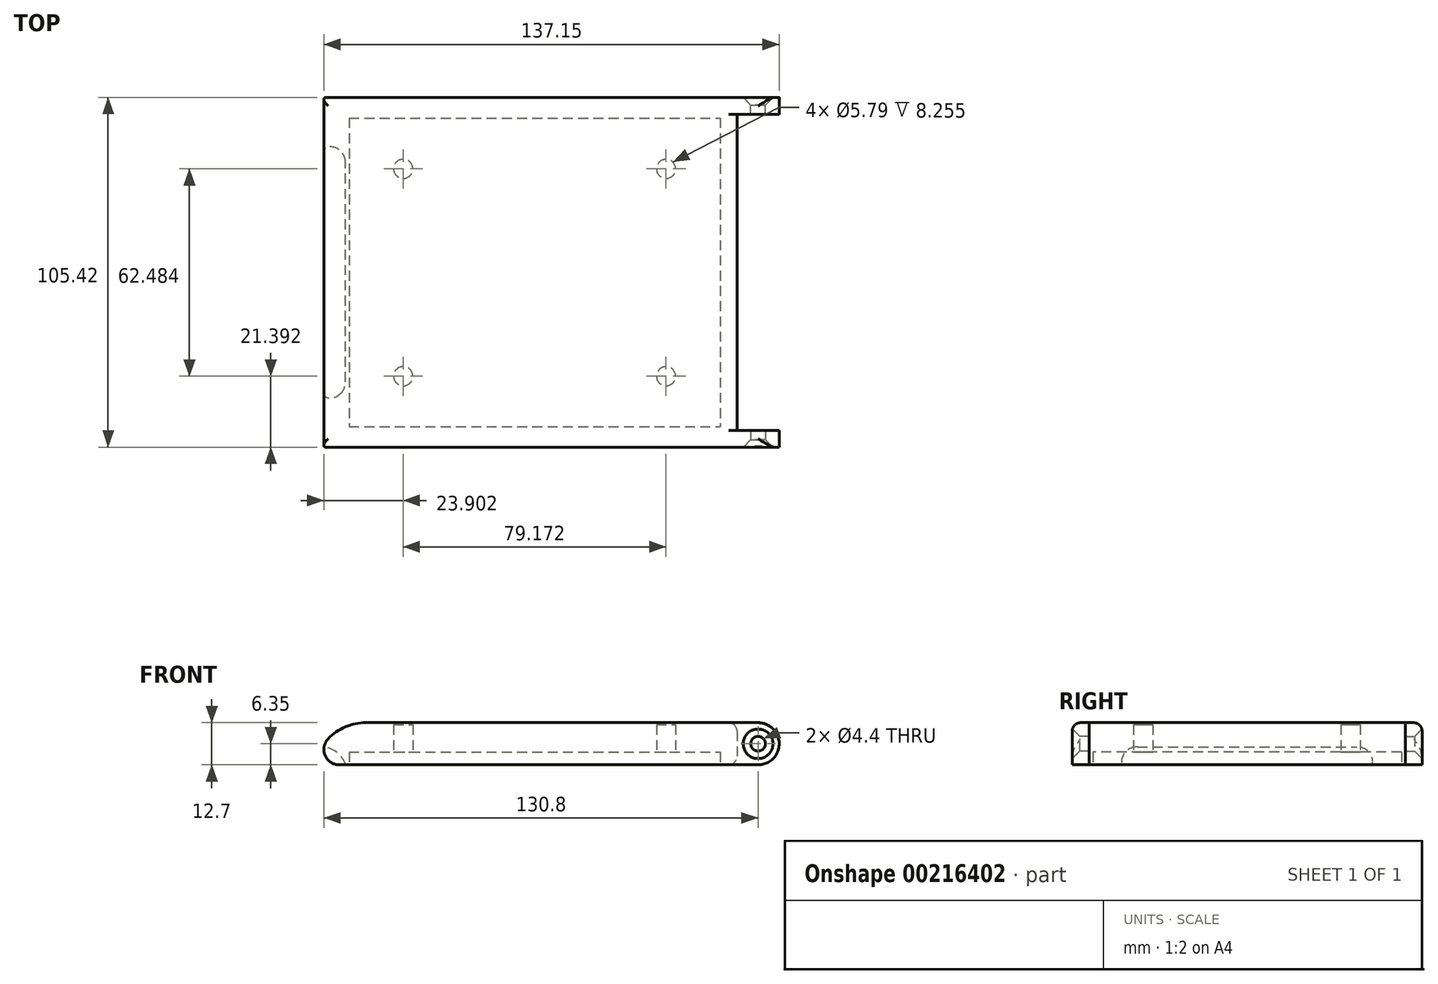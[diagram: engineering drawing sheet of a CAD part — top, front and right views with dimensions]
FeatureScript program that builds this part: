
annotation { "Feature Type Name" : "Feature", "Feature Type Description" : "" }
export const myFeature = defineFeature(function(context is Context, id is Id, definition is map)
    precondition{}
    {
        {
            var Q0;
            Q0=qCreatedBy(makeId("Front.planeOp"),FACE);
            var sketch = newSketch(context, id + "F0", { "sketchPlane" : qUnion([Q0])});
            skLineSegment(sketch, "E0", {"start": v(-6.35, 0) * mm, "end": v(-132.53, 0) * mm});
            skLineSegment(sketch, "E1", {"start": v(0, 6.35) * mm, "end": v(0, 6.35) * mm});
            skPoint(sketch, "E2.visualSharp", {"position": v(0, 12.7) * mm});
            skArc(sketch, "E2.filletArc", {"start": v(0, 6.35) * mm, "mid": v(-1.86, 10.84) * mm, "end": v(-6.35, 12.7) * mm});
            skPoint(sketch, "E3.visualSharp", {"position": v(0, 0) * mm});
            skArc(sketch, "E3.filletArc", {"start": v(-6.35, 0) * mm, "mid": v(-1.86, 1.86) * mm, "end": v(0, 6.35) * mm});
            skLineSegment(sketch, "E4", {"start": v(-6.35, 12.7) * mm, "end": v(-124.46, 12.7) * mm});
            skArc(sketch, "E5", {"start": v(-135.88, 7.81) * mm, "mid": v(-136.78, 2.8) * mm, "end": v(-132.53, 0) * mm});
            skArc(sketch, "E6", {"start": v(-124.46, 12.7) * mm, "mid": v(-130.67, 11.43) * mm, "end": v(-135.88, 7.81) * mm});
            skSolve(sketch);
        }
        {
            var Q0;
            Q0 = qSketchRegion(id + "F0", true);
            extrude(context, id + "F1", {"entities" : qUnion([Q0]), "endBound" : BoundingType.SYMMETRIC, "oppositeDirection" : true, "depth" : 105.4 * mm});
        }
        {
            var Q0;
            Q0=makeQuery(id+"F1.opExtrude","CAP_FACE",FACE,{"disambiguationData":[OSD([sQuery(id+"F0.wireOp",EDGE,"E0"),sQuery(id+"F0.wireOp",EDGE,"E1"),sQuery(id+"F0.wireOp",EDGE,"HZy6QrKH-Mdw4-o4Dm-VMrE-zzrVWmDgLelF"),sQuery(id+"F0.wireOp",EDGE,"t4Bq1xRU-PNGr-nmEO-KA5W-6uztIBIaK37j"),sQuery(id+"F0.wireOp",EDGE,"E2.filletArc"),sQuery(id+"F0.wireOp",EDGE,"E3.filletArc")])],"isStart":false});
            var sketch = newSketch(context, id + "F2", { "sketchPlane" : qUnion([Q0])});
            skPoint(sketch, "E7", {"position": v(6.35, 6.35) * mm});
            skSolve(sketch);
        }
        {
            var Q0;
            Q0=sQuery(id+"F2.wireOp",VERTEX,"E7");
            var Q1;
            Q1=makeQuery(id+"F1.opExtrude","SWEPT_BODY",BODY,{"disambiguationData":[OSD([sQuery(id+"F0.wireOp",EDGE,"E0"),sQuery(id+"F0.wireOp",EDGE,"E1"),sQuery(id+"F0.wireOp",EDGE,"HZy6QrKH-Mdw4-o4Dm-VMrE-zzrVWmDgLelF"),sQuery(id+"F0.wireOp",EDGE,"t4Bq1xRU-PNGr-nmEO-KA5W-6uztIBIaK37j"),sQuery(id+"F0.wireOp",EDGE,"E2.filletArc"),sQuery(id+"F0.wireOp",EDGE,"E3.filletArc")])]});
            hole(context, id + "F3", {"style" : HoleStyle.C_SINK, "endStyle" : HoleEndStyle.BLIND, "standardTappedOrClearance" : lookupTablePath({ "standard" : "ISO", "fit" : "Normal", "size" : "M4", "type" : "Clearance" }), "standardBlindInLast" : lookupTablePath({ "fit" : "Standard", "standard" : "ISO", "size" : "M4", "type" : "Clearance" }), "holeDiameter" : 4.4 * mm, "cSinkDiameter" : 8.96 * mm, "cSinkAngle" : 90 * degree, "holeDepth" : 25.4 * mm, "tappedDepth" : 3.96 * mm, "tapClearance" : 3, "locations" : qUnion([Q0]), "scope" : qUnion([Q1])});
        }
        {
            var Q0;
            Q0=qCreatedBy(makeId("Front.planeOp"),FACE);
            var sketch = newSketch(context, id + "F4", { "sketchPlane" : qUnion([Q0])});
            skLineSegment(sketch, "E8.bottom", {"start": v(-12.7, 13.86) * mm, "end": v(12.7, 13.86) * mm});
            skLineSegment(sketch, "E8.top", {"start": v(-12.7, -13.86) * mm, "end": v(12.7, -13.86) * mm});
            skLineSegment(sketch, "E8.left", {"start": v(-12.7, 13.86) * mm, "end": v(-12.7, -13.86) * mm});
            skLineSegment(sketch, "E8.right", {"start": v(12.7, 13.86) * mm, "end": v(12.7, -13.86) * mm});
            skPoint(sketch, "E8.middle", {"position": v(0, 0) * mm});
            skSolve(sketch);
        }
        {
            var Q0;
            Q0 = qSketchRegion(id + "F4", true);
            extrude(context, id + "F5", {"entities" : qUnion([Q0]), "operationType" : NewBodyOperationType.REMOVE, "endBound" : BoundingType.SYMMETRIC, "oppositeDirection" : true, "depth" : 95.25 * mm});
        }
        {
            var Q0;
            Q0=makeQuery(id+"F1.opExtrude","CAP_FACE",FACE,{"disambiguationData":[OSD([sQuery(id+"F0.wireOp",EDGE,"E0"),sQuery(id+"F0.wireOp",EDGE,"E1"),sQuery(id+"F0.wireOp",EDGE,"HZy6QrKH-Mdw4-o4Dm-VMrE-zzrVWmDgLelF"),sQuery(id+"F0.wireOp",EDGE,"t4Bq1xRU-PNGr-nmEO-KA5W-6uztIBIaK37j"),sQuery(id+"F0.wireOp",EDGE,"E2.filletArc"),sQuery(id+"F0.wireOp",EDGE,"E3.filletArc")])],"isStart":true});
            var sketch = newSketch(context, id + "F6", { "sketchPlane" : qUnion([Q0])});
            skPoint(sketch, "E9", {"position": v(-6.35, 6.35) * mm});
            skSolve(sketch);
        }
        {
            var Q0;
            Q0=sQuery(id+"F6.wireOp",VERTEX,"E9");
            var Q1;
            Q1=makeQuery(id+"F1.opExtrude","SWEPT_BODY",BODY,{"disambiguationData":[OSD([sQuery(id+"F0.wireOp",EDGE,"E0"),sQuery(id+"F0.wireOp",EDGE,"E1"),sQuery(id+"F0.wireOp",EDGE,"HZy6QrKH-Mdw4-o4Dm-VMrE-zzrVWmDgLelF"),sQuery(id+"F0.wireOp",EDGE,"t4Bq1xRU-PNGr-nmEO-KA5W-6uztIBIaK37j"),sQuery(id+"F0.wireOp",EDGE,"E2.filletArc"),sQuery(id+"F0.wireOp",EDGE,"E3.filletArc")])]});
            hole(context, id + "F7", {"style" : HoleStyle.C_SINK, "endStyle" : HoleEndStyle.BLIND, "standardTappedOrClearance" : lookupTablePath({ "standard" : "ISO", "fit" : "Normal", "size" : "M4", "type" : "Clearance" }), "standardBlindInLast" : lookupTablePath({ "fit" : "Standard", "standard" : "ISO", "size" : "M4", "type" : "Clearance" }), "holeDiameter" : 4.4 * mm, "cSinkDiameter" : 8.96 * mm, "cSinkAngle" : 90 * degree, "holeDepth" : 25.4 * mm, "tappedDepth" : 3.96 * mm, "tapClearance" : 3, "locations" : qUnion([Q0]), "scope" : qUnion([Q1])});
        }
        {
            var Q0;
            Q0=makeQuery(id+"F1.opExtrude","SWEPT_FACE",FACE,{"disambiguationData":[OSD([sQuery(id+"F0.wireOp",EDGE,"E0")])]});
            var sketch = newSketch(context, id + "F8", { "sketchPlane" : qUnion([Q0])});
            skLineSegment(sketch, "E10.bottom", {"start": v(-129.54, -46.48) * mm, "end": v(-17.78, -46.48) * mm});
            skLineSegment(sketch, "E10.top", {"start": v(-129.54, 46.48) * mm, "end": v(-17.78, 46.48) * mm});
            skLineSegment(sketch, "E10.left", {"start": v(-129.54, -46.48) * mm, "end": v(-129.54, 46.48) * mm});
            skLineSegment(sketch, "E10.right", {"start": v(-17.78, -46.48) * mm, "end": v(-17.78, 46.48) * mm});
            skPoint(sketch, "E11", {"position": v(-17.78, 0) * mm});
            skLineSegment(sketch, "E12", {"start": v(-17.78, 0) * mm, "end": v(-12.7, 0) * mm});
            skSolve(sketch);
        }
        {
            var Q0;
            Q0 = qSketchRegion(id + "F8", true);
            extrude(context, id + "F9", {"entities" : qUnion([Q0]), "operationType" : NewBodyOperationType.REMOVE, "oppositeDirection" : true, "depth" : 3.8 * mm});
        }
        {
            var Q0;
            Q0=makeQuery(id+"F9.boolean.opBoolean","COPY",FACE,{"derivedFrom":makeQuery(id+"F9.opExtrude","CAP_FACE",FACE,{"disambiguationData":[OSD([sQuery(id+"F8.wireOp",EDGE,"E10.bottom"),sQuery(id+"F8.wireOp",EDGE,"E10.top"),sQuery(id+"F8.wireOp",EDGE,"E10.left"),sQuery(id+"F8.wireOp",EDGE,"E10.right")])],"isStart":false})});
            var sketch = newSketch(context, id + "F10", { "sketchPlane" : qUnion([Q0])});
            skPoint(sketch, "E13", {"position": v(-113.25, -31.17) * mm});
            skPoint(sketch, "E14.0.1.0", {"position": v(-113.25, 31.32) * mm});
            skPoint(sketch, "E14.1.0.0", {"position": v(-34.08, -31.17) * mm});
            skPoint(sketch, "E14.1.1.0", {"position": v(-34.08, 31.32) * mm});
            skLineSegment(sketch, "E14.direction1", {"start": v(-113.25, -31.17) * mm, "end": v(-34.08, -31.17) * mm, "construction": true});
            skLineSegment(sketch, "E14.direction2", {"start": v(-113.25, -31.17) * mm, "end": v(-113.25, 31.32) * mm, "construction": true});
            skCircle(sketch, "E15", {"center": v(-113.25, -31.17) * mm, "radius": 2.9 * mm});
            skCircle(sketch, "E16", {"center": v(-113.25, 31.32) * mm, "radius": 2.9 * mm});
            skCircle(sketch, "E17", {"center": v(-34.08, 31.32) * mm, "radius": 2.9 * mm});
            skCircle(sketch, "E18", {"center": v(-34.08, -31.17) * mm, "radius": 2.9 * mm});
            skSolve(sketch);
        }
        {
            var Q0;
            Q0 = qSketchRegion(id + "F10", true);
            extrude(context, id + "F11", {"entities" : qUnion([Q0]), "operationType" : NewBodyOperationType.REMOVE, "oppositeDirection" : true, "depth" : 8.25 * mm});
        }
        {
            var Q0;
            Q0=makeQuery(id+"F1.opExtrude","CAP_EDGE",EDGE,{"disambiguationData":[OSD([sQuery(id+"F0.wireOp",EDGE,"E4")])],"isStart":true});
            var Q1;
            Q1=makeQuery(id+"F1.opExtrude","CAP_EDGE",EDGE,{"disambiguationData":[OSD([sQuery(id+"F0.wireOp",EDGE,"E4")])],"isStart":false});
            var Q2;
            Q2=makeQuery(id+"F1.opExtrude","CAP_EDGE",EDGE,{"disambiguationData":[OSD([sQuery(id+"F0.wireOp",EDGE,"E6")])],"isStart":false});
            var Q3;
            Q3=makeQuery(id+"F1.opExtrude","CAP_EDGE",EDGE,{"disambiguationData":[OSD([sQuery(id+"F0.wireOp",EDGE,"E6")])],"isStart":true});
            fillet(context, id + "F12", {"entities" : qUnion([Q0, Q1, Q2, Q3]), "radius" : 2.54 * mm, "allowEdgeOverflow" : false});
        }
        {
            var Q0;
            Q0=qCreatedBy(makeId("Front.planeOp"),FACE);
            var sketch = newSketch(context, id + "F13", { "sketchPlane" : qUnion([Q0])});
            skLineSegment(sketch, "E19", {"start": v(-130.28, -3.45) * mm, "end": v(-139.17, -3.45) * mm});
            skLineSegment(sketch, "E20", {"start": v(-139.17, -3.45) * mm, "end": v(-139.17, 5.44) * mm});
            skArc(sketch, "E21", {"start": v(-130.28, -3.45) * mm, "mid": v(-132.57, 3.16) * mm, "end": v(-139.17, 5.44) * mm});
            skSolve(sketch);
        }
        {
            var Q0;
            Q0 = qSketchRegion(id + "F13", true);
            extrude(context, id + "F14", {"entities" : qUnion([Q0]), "operationType" : NewBodyOperationType.REMOVE, "endBound" : BoundingType.SYMMETRIC, "depth" : 76.2 * mm});
        }
        {
            var Q0;
            Q0=makeQuery(id+"F14.boolean.opBoolean","COPY",EDGE,{"derivedFrom":makeQuery(id+"F14.opExtrude","CAP_EDGE",EDGE,{"disambiguationData":[OSD([sQuery(id+"F13.wireOp",EDGE,"E21")])],"isStart":true})});
            var Q1;
            Q1=makeQuery(id+"F14.boolean.opBoolean","COPY",EDGE,{"derivedFrom":makeQuery(id+"F14.opExtrude","CAP_EDGE",EDGE,{"disambiguationData":[OSD([sQuery(id+"F13.wireOp",EDGE,"E21")])],"isStart":false})});
            fillet(context, id + "F15", {"entities" : qUnion([Q0, Q1]), "radius" : 5.08 * mm, "tangentPropagation" : true, "allowEdgeOverflow" : false});
        }
        {
            var Q0;
            Q0=makeQuery(id+"F5.boolean.opBoolean","INTERSECT",EDGE,{"derivedFrom":[makeQuery(id+"F1.opExtrude","SWEPT_FACE",FACE,{"disambiguationData":[OSD([sQuery(id+"F0.wireOp",EDGE,"E4")])]}),makeQuery(id+"F5.opExtrude","SWEPT_FACE",FACE,{"disambiguationData":[OSD([sQuery(id+"F4.wireOp",EDGE,"E8.left")])]})]});
            var Q1;
            Q1=makeQuery(id+"F5.boolean.opBoolean","INTERSECT",EDGE,{"derivedFrom":[makeQuery(id+"F1.opExtrude","SWEPT_FACE",FACE,{"disambiguationData":[OSD([sQuery(id+"F0.wireOp",EDGE,"E0")])]}),makeQuery(id+"F5.opExtrude","SWEPT_FACE",FACE,{"disambiguationData":[OSD([sQuery(id+"F4.wireOp",EDGE,"E8.left")])]})]});
            fillet(context, id + "F16", {"entities" : qUnion([Q0, Q1]), "radius" : 2.54 * mm, "tangentPropagation" : true, "allowEdgeOverflow" : false});
        }
    });
